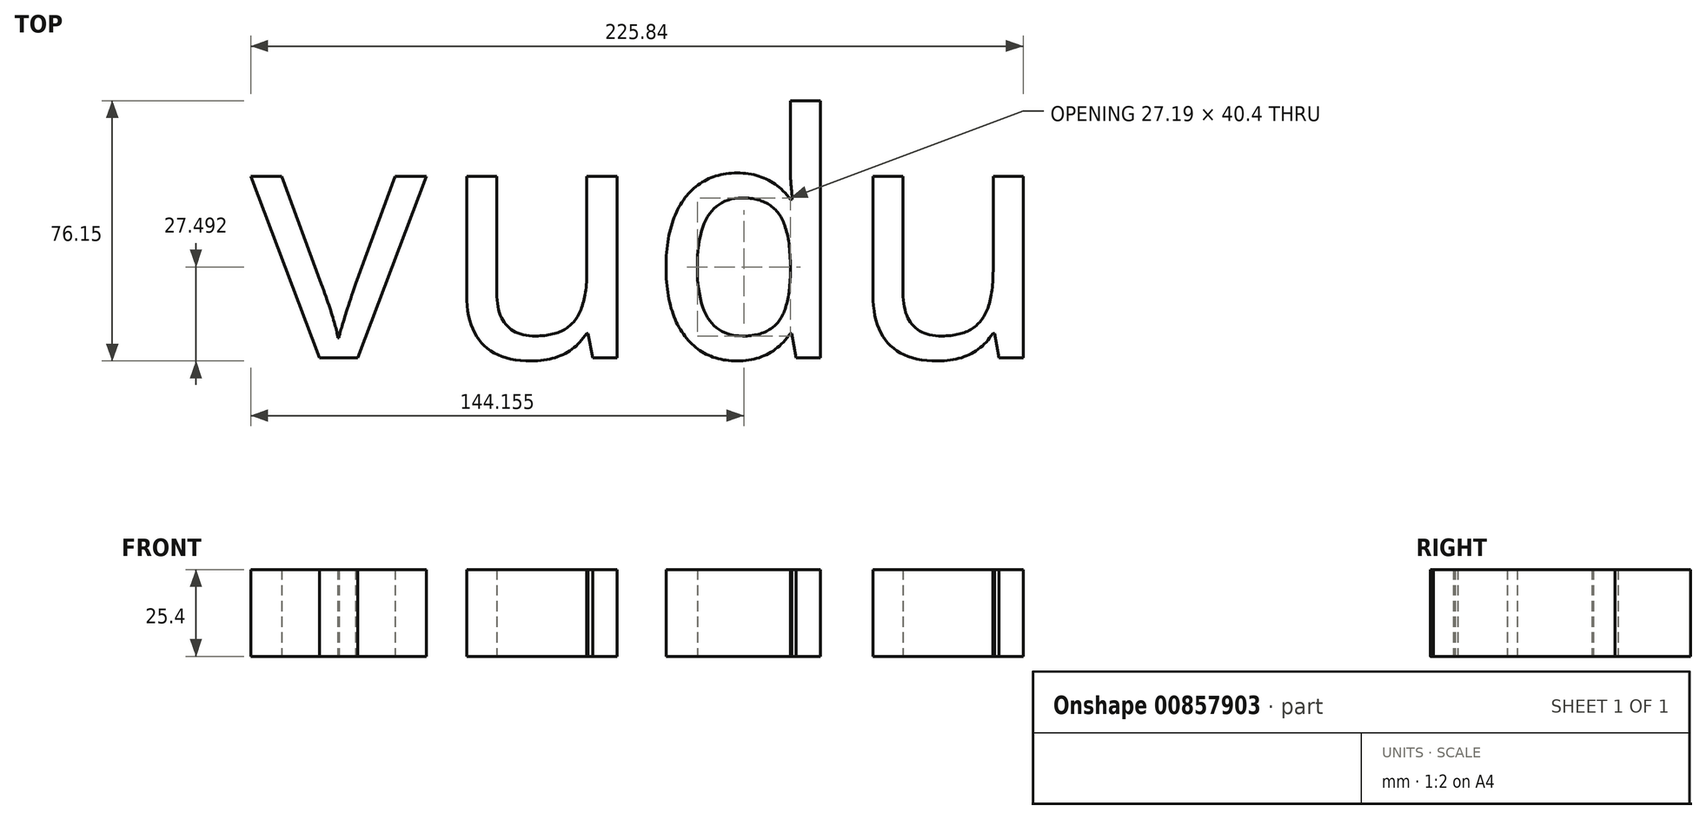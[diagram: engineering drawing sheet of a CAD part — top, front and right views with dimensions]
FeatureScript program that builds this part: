
annotation { "Feature Type Name" : "Feature", "Feature Type Description" : "" }
export const myFeature = defineFeature(function(context is Context, id is Id, definition is map)
    precondition{}
    {
        {
            var Q0;
            Q0=qCreatedBy(makeId("Top.planeOp"),FACE);
            var sketch = newSketch(context, id + "F0", { "sketchPlane" : qUnion([Q0])});
            skText(sketch, "E0", { "text": "vudu", "fontName": "DroidSansMono.ttf"});
            const initialGuessF0  = {"E0": [0, 0, 1, 0, 0.07124]};
            skSetInitialGuess(sketch, initialGuessF0);
            skSolve(sketch);
        }
        {
            var Q0;
            Q0 = qSketchRegion(id + "F0", true);
            extrude(context, id + "F1", {"entities" : qUnion([Q0]), "depth" : 25.4 * mm, "offsetDistance" : 25.4 * mm});
        }
    });
